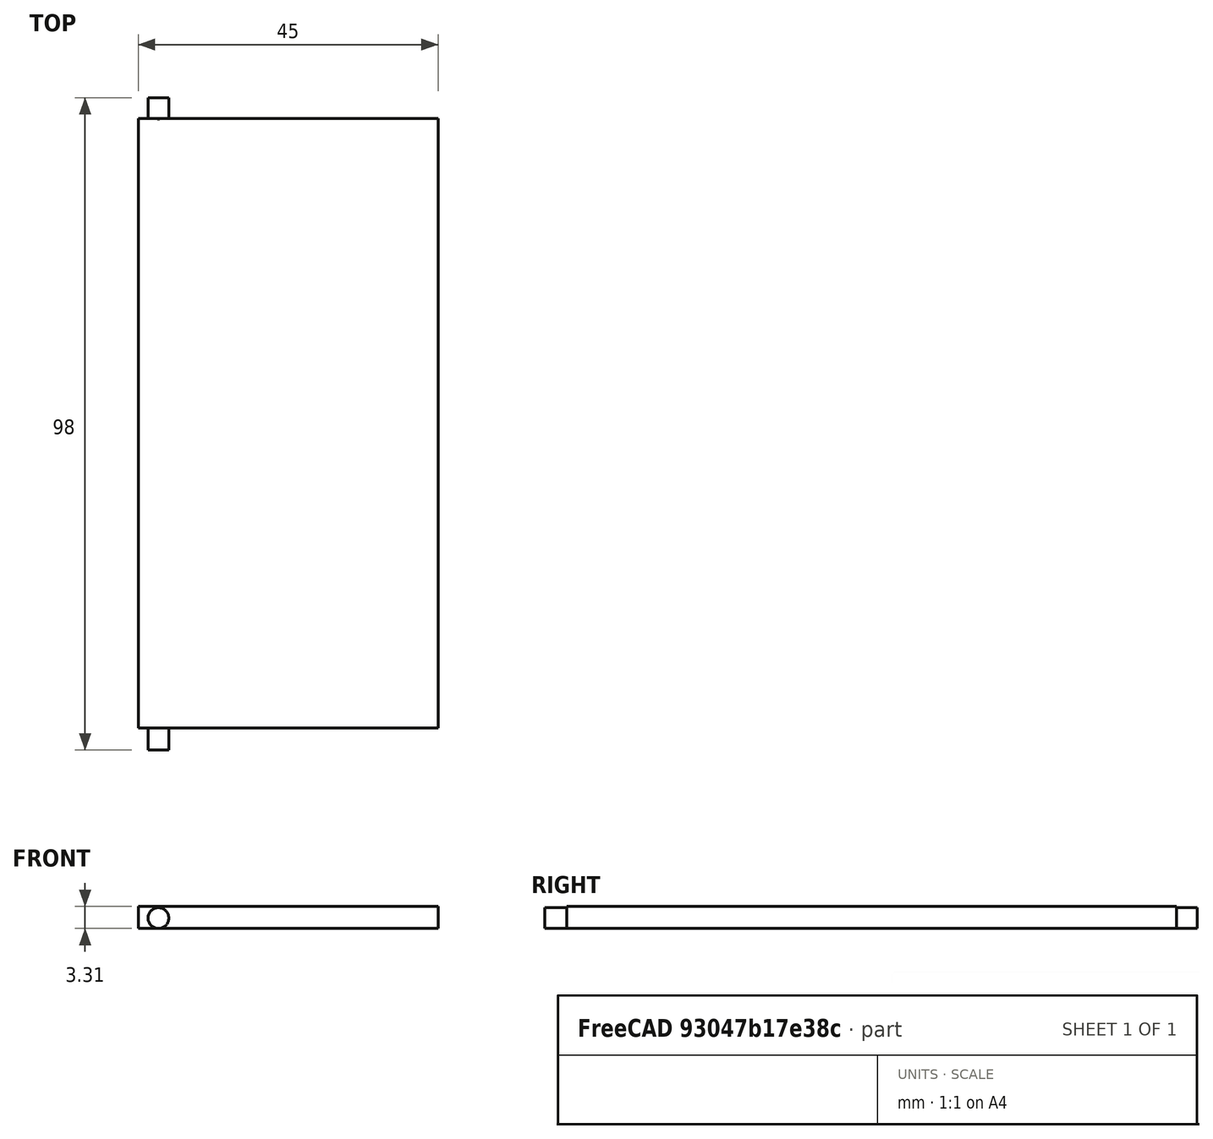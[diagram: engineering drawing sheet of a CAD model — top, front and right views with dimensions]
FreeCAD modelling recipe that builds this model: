
FCSTD DOCUMENT  (FreeCAD 0.20R29603 (Git))
Label: shuffle-flap-short
License: All rights reserved
LicenseURL: http://en.wikipedia.org/wiki/All_rights_reserved
objects: PartDesign::AdditiveCylinder×2, PartDesign::AdditiveBox×1, PartDesign::Body×1
note: 7 computed .brp shape members not serialized (recipe doc carries the construction recipe); baked Part::Feature solids carry a one-line shape summary decoded from their .brp

FEATURE [PartDesign::AdditiveBox] Box
  AttacherType = Attacher::AttachEngine3D
  Height = 3.3
  Length = 45
  Width = 91.6
FEATURE [PartDesign::AdditiveCylinder] Cylinder
  Angle = 360
  AttacherType = Attacher::AttachEngine3D
  AttachmentOffset = pos=(3,1.55,0) rot=(0,0,1;0rad)
  BaseFeature = -> Box
  FirstAngle = 0
  Height = 3.3
  MapMode = 5
  Placement = pos=(3,3e-16,1.55) rot=(1,0,0;1.5708rad)
  Radius = 1.56
  SecondAngle = 0
  Support = -> [Box]
FEATURE [PartDesign::AdditiveCylinder] Cylinder001
  Angle = 360
  AttacherType = Attacher::AttachEngine3D
  AttachmentOffset = pos=(0,0,-98) rot=(0,0,1;0rad)
  BaseFeature = -> Cylinder
  FirstAngle = 0
  Height = 3.3
  MapMode = 5
  Placement = pos=(3,94.7,1.55) rot=(1,0,0;1.5708rad)
  Radius = 1.56
  SecondAngle = 0
  Support = -> [Cylinder]
FEATURE [PartDesign::Body] Body
  Group = -> [Box,Cylinder,Cylinder001]
  Origin = -> Origin
  Tip = -> Cylinder001
